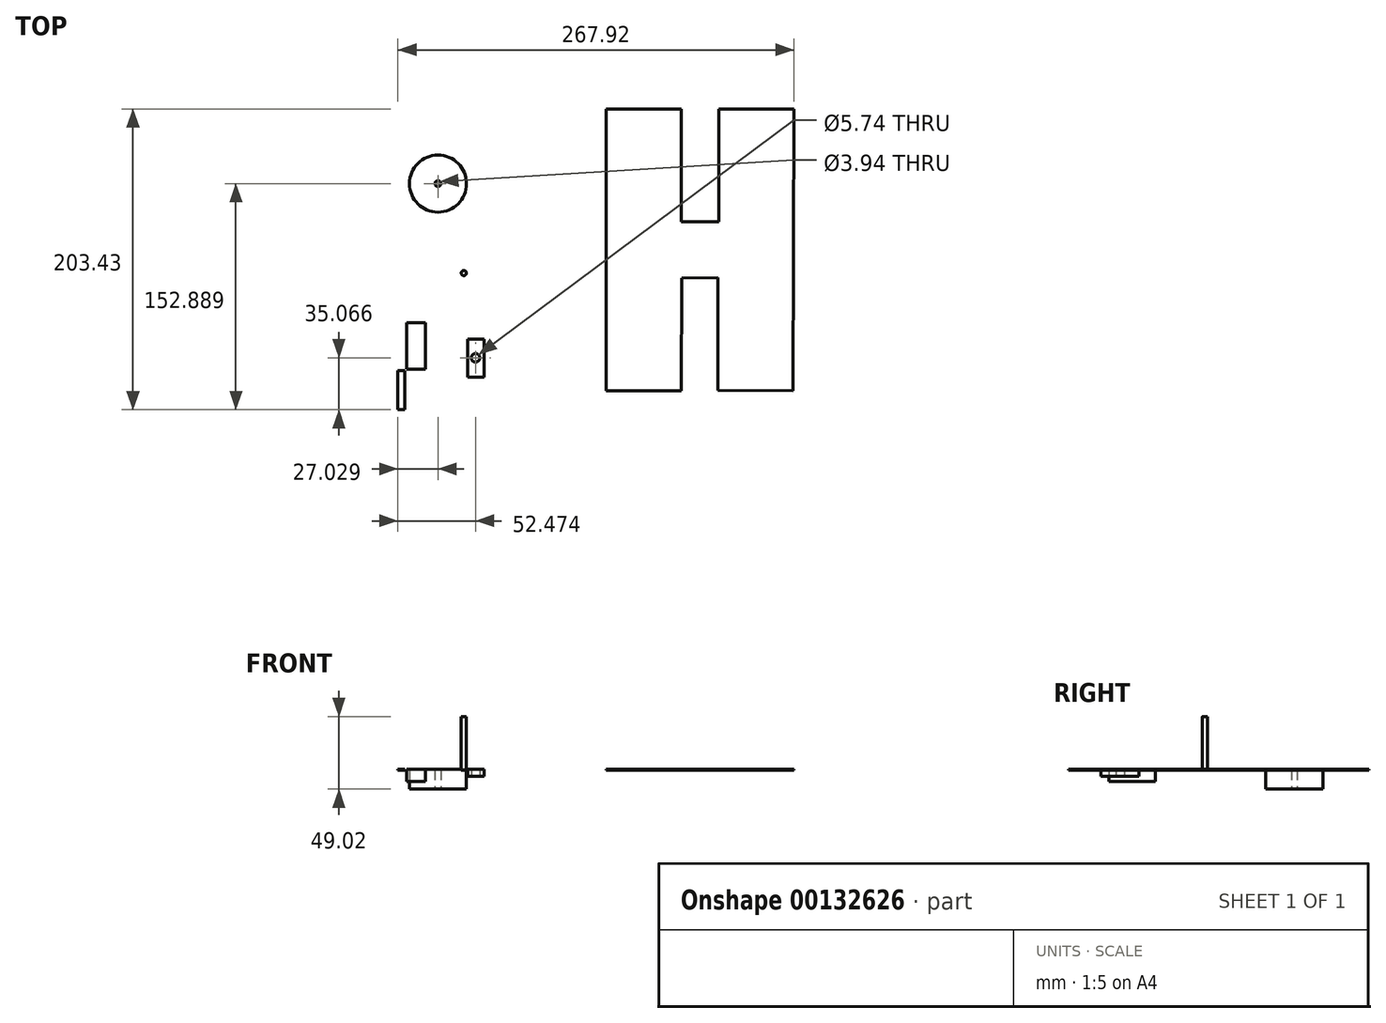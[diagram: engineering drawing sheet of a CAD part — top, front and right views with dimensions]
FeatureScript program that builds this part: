
annotation { "Feature Type Name" : "Feature", "Feature Type Description" : "" }
export const myFeature = defineFeature(function(context is Context, id is Id, definition is map)
    precondition{}
    {
        {
            var Q0;
            Q0=qCreatedBy(makeId("Top.planeOp"),FACE);
            var sketch = newSketch(context, id + "F0", { "sketchPlane" : qUnion([Q0])});
            skLineSegment(sketch, "E0", {"start": v(-70, 151.5) * mm, "end": v(-19.2, 151.5) * mm});
            skLineSegment(sketch, "E1", {"start": v(-70, 151.5) * mm, "end": v(-70, -39) * mm});
            skLineSegment(sketch, "E2", {"start": v(-70, -39) * mm, "end": v(-19.2, -39) * mm});
            skLineSegment(sketch, "E3", {"start": v(-19.2, 151.5) * mm, "end": v(-19.2, 75.38) * mm});
            skLineSegment(sketch, "E4", {"start": v(-19.2, 75.38) * mm, "end": v(6.2, 75.38) * mm});
            skLineSegment(sketch, "E5", {"start": v(5.52, -38.8) * mm, "end": v(56.32, -39) * mm});
            skLineSegment(sketch, "E6", {"start": v(56.32, -39) * mm, "end": v(57.06, 151.5) * mm});
            skLineSegment(sketch, "E7", {"start": v(6.2, 75.38) * mm, "end": v(6.2, 151.58) * mm});
            skLineSegment(sketch, "E8", {"start": v(6.2, 151.58) * mm, "end": v(57.06, 151.5) * mm});
            skLineSegment(sketch, "E9", {"start": v(-19.2, -39) * mm, "end": v(-18.9, 37.2) * mm});
            skLineSegment(sketch, "E10", {"start": v(5.52, -38.8) * mm, "end": v(5.52, 37.4) * mm});
            skLineSegment(sketch, "E11", {"start": v(-18.9, 37.2) * mm, "end": v(5.52, 37.4) * mm});
            skCircle(sketch, "E12", {"center": v(-166.3, 40.57) * mm, "radius": 1.73 * mm});
            skCircle(sketch, "E13", {"center": v(-183.83, 101.04) * mm, "radius": 19.3 * mm});
            skCircle(sketch, "E14", {"center": v(-183.83, 101.04) * mm, "radius": 1.97 * mm});
            skLineSegment(sketch, "E15.bottom", {"start": v(-163.56, -29.95) * mm, "end": v(-152.7, -29.95) * mm});
            skLineSegment(sketch, "E15.top", {"start": v(-163.56, -3.98) * mm, "end": v(-152.7, -3.98) * mm});
            skLineSegment(sketch, "E15.left", {"start": v(-163.56, -29.95) * mm, "end": v(-163.56, -3.98) * mm});
            skLineSegment(sketch, "E15.right", {"start": v(-152.7, -29.95) * mm, "end": v(-152.7, -3.98) * mm});
            skCircle(sketch, "E16", {"center": v(-158.39, -16.78) * mm, "radius": 2.87 * mm});
            skLineSegment(sketch, "E17.bottom", {"start": v(-205.05, -24.34) * mm, "end": v(-192.44, -24.34) * mm});
            skLineSegment(sketch, "E17.top", {"start": v(-205.05, 7.05) * mm, "end": v(-192.44, 7.05) * mm});
            skLineSegment(sketch, "E17.left", {"start": v(-205.05, -24.34) * mm, "end": v(-205.05, 7.05) * mm});
            skLineSegment(sketch, "E17.right", {"start": v(-192.44, -24.34) * mm, "end": v(-192.44, 7.05) * mm});
            skLineSegment(sketch, "E18.bottom", {"start": v(-206.18, -51.85) * mm, "end": v(-210.86, -51.85) * mm});
            skLineSegment(sketch, "E18.top", {"start": v(-206.18, -25.5) * mm, "end": v(-210.86, -25.5) * mm});
            skLineSegment(sketch, "E18.left", {"start": v(-206.18, -51.85) * mm, "end": v(-206.18, -25.5) * mm});
            skLineSegment(sketch, "E18.right", {"start": v(-210.86, -51.85) * mm, "end": v(-210.86, -25.5) * mm});
            skSolve(sketch);
        }
        {
            var Q0;
            Q0 = qSketchRegion(id + "F0", true);
            extrude(context, id + "F1", {"entities" : qUnion([Q0]), "depth" : 0.76 * mm});
        }
        {
            var Q0;
            Q0=makeQuery(id+"F1.opExtrude","CAP_FACE",FACE,{"disambiguationData":[OSD([sQuery(id+"F0.wireOp",EDGE,"E12")])],"isStart":false});
            extrude(context, id + "F2", {"entities" : qUnion([Q0]), "operationType" : NewBodyOperationType.ADD, "depth" : 35.56 * mm});
        }
        {
            var Q0;
            Q0=makeQuery(id+"F1.opExtrude","CAP_FACE",FACE,{"disambiguationData":[OSD([sQuery(id+"F0.wireOp",EDGE,"E13"),sQuery(id+"F0.wireOp",EDGE,"E14")])],"isStart":true});
            extrude(context, id + "F3", {"entities" : qUnion([Q0]), "operationType" : NewBodyOperationType.ADD, "depth" : 12.7 * mm});
        }
        {
            var Q0;
            Q0=makeQuery(id+"F1.opExtrude","CAP_FACE",FACE,{"disambiguationData":[OSD([sQuery(id+"F0.wireOp",EDGE,"E15.bottom"),sQuery(id+"F0.wireOp",EDGE,"E15.top"),sQuery(id+"F0.wireOp",EDGE,"E15.left"),sQuery(id+"F0.wireOp",EDGE,"E15.right"),sQuery(id+"F0.wireOp",EDGE,"E16")])],"isStart":true});
            extrude(context, id + "F4", {"entities" : qUnion([Q0]), "operationType" : NewBodyOperationType.ADD, "depth" : 4.2 * mm});
        }
        {
            var Q0;
            Q0=makeQuery(id+"F1.opExtrude","CAP_FACE",FACE,{"disambiguationData":[OSD([sQuery(id+"F0.wireOp",EDGE,"E17.bottom"),sQuery(id+"F0.wireOp",EDGE,"E17.top"),sQuery(id+"F0.wireOp",EDGE,"E17.left"),sQuery(id+"F0.wireOp",EDGE,"E17.right")])],"isStart":true});
            extrude(context, id + "F5", {"entities" : qUnion([Q0]), "operationType" : NewBodyOperationType.ADD, "depth" : 7.62 * mm});
        }
    });
